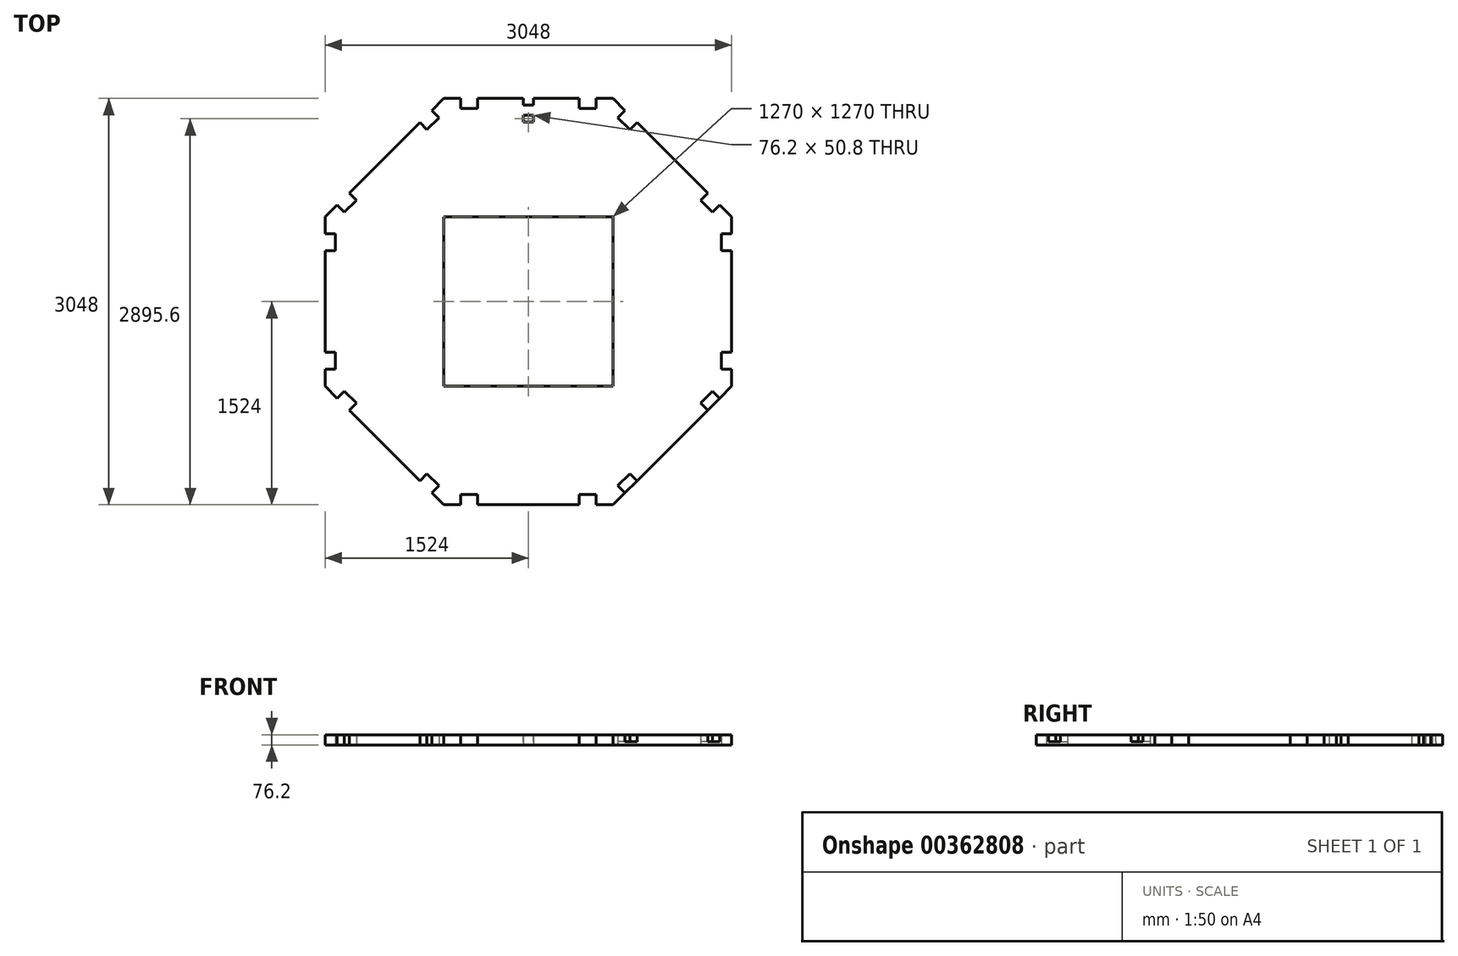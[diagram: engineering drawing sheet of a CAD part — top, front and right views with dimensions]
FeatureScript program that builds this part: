
annotation { "Feature Type Name" : "Feature", "Feature Type Description" : "" }
export const myFeature = defineFeature(function(context is Context, id is Id, definition is map)
    precondition{}
    {
        {
            var Q0;
            Q0=qCreatedBy(makeId("Top.planeOp"),FACE);
            var sketch = newSketch(context, id + "F0", { "sketchPlane" : qUnion([Q0])});
            skLineSegment(sketch, "E0.bottom", {"start": v(-635, 635) * mm, "end": v(635, 635) * mm});
            skLineSegment(sketch, "E0.top", {"start": v(-635, -635) * mm, "end": v(635, -635) * mm});
            skLineSegment(sketch, "E0.left", {"start": v(-1524, 635) * mm, "end": v(-1524, 508) * mm});
            skLineSegment(sketch, "E0.right", {"start": v(1524, 635) * mm, "end": v(1524, 508) * mm});
            skPoint(sketch, "E0.middle", {"position": v(0, 0) * mm});
            skLineSegment(sketch, "E1.bottom", {"start": v(-635, 1524) * mm, "end": v(-508, 1524) * mm});
            skLineSegment(sketch, "E1.top", {"start": v(-635, -1524) * mm, "end": v(-508, -1524) * mm});
            skLineSegment(sketch, "E1.left", {"start": v(-635, 635) * mm, "end": v(-635, -635) * mm});
            skLineSegment(sketch, "E1.right", {"start": v(635, 635) * mm, "end": v(635, -635) * mm});
            skLineSegment(sketch, "E2", {"start": v(-635, 1524) * mm, "end": v(-724.8, 1434.2) * mm});
            skLineSegment(sketch, "E3", {"start": v(-1524, -635) * mm, "end": v(-1434.2, -724.8) * mm});
            skLineSegment(sketch, "E4", {"start": v(635, -1524) * mm, "end": v(1524, -635) * mm});
            skLineSegment(sketch, "E5", {"start": v(1524, 635) * mm, "end": v(1434.2, 724.8) * mm});
            skLineSegment(sketch, "E6", {"start": v(-508, 1524) * mm, "end": v(-508, 1447.8) * mm});
            skLineSegment(sketch, "E7", {"start": v(-508, 1447.8) * mm, "end": v(-381, 1447.8) * mm});
            skLineSegment(sketch, "E8", {"start": v(-381, 1447.8) * mm, "end": v(-381, 1524) * mm});
            skLineSegment(sketch, "E9", {"start": v(635, 1524) * mm, "end": v(508, 1524) * mm});
            skLineSegment(sketch, "E10", {"start": v(508, 1524) * mm, "end": v(508, 1447.8) * mm});
            skLineSegment(sketch, "E11", {"start": v(508, 1447.8) * mm, "end": v(381, 1447.8) * mm});
            skLineSegment(sketch, "E12", {"start": v(381, 1447.8) * mm, "end": v(381, 1524) * mm});
            skLineSegment(sketch, "E13", {"start": v(-38.1, 1524) * mm, "end": v(-38.1, 1473.2) * mm});
            skLineSegment(sketch, "E14", {"start": v(38.1, 1524) * mm, "end": v(38.1, 1473.2) * mm});
            skLineSegment(sketch, "E15", {"start": v(38.1, 1473.2) * mm, "end": v(-38.1, 1473.2) * mm});
            skLineSegment(sketch, "E16", {"start": v(-38.1, 1473.2) * mm, "end": v(-38.1, 1397) * mm});
            skLineSegment(sketch, "E17", {"start": v(38.1, 1473.2) * mm, "end": v(38.1, 1397) * mm});
            skLineSegment(sketch, "E18", {"start": v(38.1, 1397) * mm, "end": v(-38.1, 1397) * mm});
            skLineSegment(sketch, "E19", {"start": v(-38.1, 1397) * mm, "end": v(-38.1, 1346.2) * mm});
            skLineSegment(sketch, "E20", {"start": v(38.1, 1397) * mm, "end": v(38.1, 1346.2) * mm});
            skLineSegment(sketch, "E21", {"start": v(38.1, 1346.2) * mm, "end": v(-38.1, 1346.2) * mm});
            skLineSegment(sketch, "E22", {"start": v(-38.1, 1397) * mm, "end": v(38.1, 1397) * mm});
            skLineSegment(sketch, "E23.trimOffspring", {"start": v(-381, 1524) * mm, "end": v(-38.1, 1524) * mm});
            skLineSegment(sketch, "E24.trimOffspring", {"start": v(508, 1524) * mm, "end": v(635, 1524) * mm});
            skLineSegment(sketch, "E25.trimOffspring", {"start": v(38.1, 1524) * mm, "end": v(381, 1524) * mm});
            skPoint(sketch, "E26.orphan", {"position": v(0, 1524) * mm});
            skLineSegment(sketch, "E27", {"start": v(-1524, 635) * mm, "end": v(-1434.2, 724.8) * mm});
            skLineSegment(sketch, "E28", {"start": v(-1434.2, 724.8) * mm, "end": v(-1380.32, 670.92) * mm});
            skLineSegment(sketch, "E29", {"start": v(-1380.32, 670.92) * mm, "end": v(-1290.51, 760.72) * mm});
            skLineSegment(sketch, "E30", {"start": v(-1290.51, 760.72) * mm, "end": v(-1344.4, 814.6) * mm});
            skLineSegment(sketch, "E31.trimOffspring", {"start": v(-1434.2, 724.8) * mm, "end": v(-1524, 635) * mm});
            skLineSegment(sketch, "E32", {"start": v(-724.8, 1434.2) * mm, "end": v(-670.92, 1380.32) * mm});
            skLineSegment(sketch, "E33", {"start": v(-670.92, 1380.32) * mm, "end": v(-760.72, 1290.51) * mm});
            skLineSegment(sketch, "E34", {"start": v(-760.72, 1290.51) * mm, "end": v(-814.6, 1344.4) * mm});
            skLineSegment(sketch, "E35.trimOffspring", {"start": v(-814.6, 1344.4) * mm, "end": v(-1344.4, 814.6) * mm});
            skLineSegment(sketch, "E36", {"start": v(635, 1524) * mm, "end": v(724.8, 1434.2) * mm});
            skLineSegment(sketch, "E37", {"start": v(724.8, 1434.2) * mm, "end": v(670.92, 1380.32) * mm});
            skLineSegment(sketch, "E38", {"start": v(670.92, 1380.32) * mm, "end": v(760.72, 1290.51) * mm});
            skLineSegment(sketch, "E39", {"start": v(760.72, 1290.51) * mm, "end": v(814.6, 1344.4) * mm});
            skLineSegment(sketch, "E40.trimOffspring", {"start": v(724.8, 1434.2) * mm, "end": v(635, 1524) * mm});
            skLineSegment(sketch, "E41", {"start": v(1434.2, 724.8) * mm, "end": v(1380.32, 670.92) * mm});
            skLineSegment(sketch, "E42", {"start": v(1380.32, 670.92) * mm, "end": v(1290.51, 760.72) * mm});
            skLineSegment(sketch, "E43", {"start": v(1290.51, 760.72) * mm, "end": v(1344.4, 814.6) * mm});
            skLineSegment(sketch, "E44.trimOffspring", {"start": v(1344.4, 814.6) * mm, "end": v(814.6, 1344.4) * mm});
            skLineSegment(sketch, "E45", {"start": v(-38.1, 1473.2) * mm, "end": v(38.1, 1473.2) * mm});
            skLineSegment(sketch, "E46", {"start": v(-1524, 508) * mm, "end": v(-1447.8, 508) * mm});
            skLineSegment(sketch, "E47", {"start": v(-1447.8, 508) * mm, "end": v(-1447.8, 381) * mm});
            skLineSegment(sketch, "E48", {"start": v(-1447.8, 381) * mm, "end": v(-1524, 381) * mm});
            skLineSegment(sketch, "E49.trimOffspring", {"start": v(-1524, 381) * mm, "end": v(-1524, -381) * mm});
            skLineSegment(sketch, "E50", {"start": v(-1524, -635) * mm, "end": v(-1524, -508) * mm});
            skLineSegment(sketch, "E51", {"start": v(-1524, -508) * mm, "end": v(-1447.8, -508) * mm});
            skLineSegment(sketch, "E52", {"start": v(-1447.8, -508) * mm, "end": v(-1447.8, -381) * mm});
            skLineSegment(sketch, "E53", {"start": v(-1447.8, -381) * mm, "end": v(-1524, -381) * mm});
            skLineSegment(sketch, "E54.trimOffspring", {"start": v(-1524, -508) * mm, "end": v(-1524, -635) * mm});
            skLineSegment(sketch, "E55", {"start": v(0, 1524) * mm, "end": v(0, 1397) * mm});
            skLineSegment(sketch, "E56.MirrorCS", {"start": v(1524, 508) * mm, "end": v(1447.8, 508) * mm});
            skLineSegment(sketch, "E57.MirrorCS", {"start": v(1434.2, 724.8) * mm, "end": v(1524, 635) * mm});
            skLineSegment(sketch, "E58.MirrorCS", {"start": v(1524, -508) * mm, "end": v(1524, -635) * mm});
            skLineSegment(sketch, "E59.MirrorCS", {"start": v(1524, -635) * mm, "end": v(1524, -508) * mm});
            skLineSegment(sketch, "E60.MirrorCS", {"start": v(1524, -508) * mm, "end": v(1447.8, -508) * mm});
            skLineSegment(sketch, "E61.MirrorCS", {"start": v(1447.8, 508) * mm, "end": v(1447.8, 381) * mm});
            skLineSegment(sketch, "E62.MirrorCS", {"start": v(1447.8, 381) * mm, "end": v(1524, 381) * mm});
            skLineSegment(sketch, "E63.MirrorCS", {"start": v(1447.8, -381) * mm, "end": v(1524, -381) * mm});
            skLineSegment(sketch, "E64.MirrorCS", {"start": v(1447.8, -508) * mm, "end": v(1447.8, -381) * mm});
            skLineSegment(sketch, "E65.MirrorCS", {"start": v(381, 1524) * mm, "end": v(38.1, 1524) * mm});
            skLineSegment(sketch, "E66.MirrorCS", {"start": v(1524, -635) * mm, "end": v(635, -1524) * mm});
            skLineSegment(sketch, "E67.MirrorCS", {"start": v(814.6, 1344.4) * mm, "end": v(1344.4, 814.6) * mm});
            skLineSegment(sketch, "E68.MirrorCS", {"start": v(1524, 381) * mm, "end": v(1524, -381) * mm});
            skLineSegment(sketch, "E69", {"start": v(-1434.2, -724.8) * mm, "end": v(-1524, -635) * mm});
            skLineSegment(sketch, "E70", {"start": v(-1434.2, -724.8) * mm, "end": v(-1380.32, -670.92) * mm});
            skLineSegment(sketch, "E71", {"start": v(-1380.32, -670.92) * mm, "end": v(-1290.51, -760.72) * mm});
            skLineSegment(sketch, "E72", {"start": v(-1290.51, -760.72) * mm, "end": v(-1344.4, -814.6) * mm});
            skLineSegment(sketch, "E73.trimOffspring", {"start": v(-1344.4, -814.6) * mm, "end": v(-814.6, -1344.4) * mm});
            skLineSegment(sketch, "E74", {"start": v(-635, -1524) * mm, "end": v(-724.8, -1434.2) * mm});
            skLineSegment(sketch, "E75", {"start": v(-724.8, -1434.2) * mm, "end": v(-670.92, -1380.32) * mm});
            skLineSegment(sketch, "E76", {"start": v(-670.92, -1380.32) * mm, "end": v(-760.72, -1290.51) * mm});
            skLineSegment(sketch, "E77", {"start": v(-760.72, -1290.51) * mm, "end": v(-814.6, -1344.4) * mm});
            skLineSegment(sketch, "E78.trimOffspring", {"start": v(-724.8, -1434.2) * mm, "end": v(-635, -1524) * mm});
            skLineSegment(sketch, "E79.MirrorCS", {"start": v(635, -1524) * mm, "end": v(724.8, -1434.2) * mm});
            skLineSegment(sketch, "E80.MirrorCS", {"start": v(724.8, -1434.2) * mm, "end": v(635, -1524) * mm});
            skLineSegment(sketch, "E81.MirrorCS", {"start": v(1434.2, -724.8) * mm, "end": v(1524, -635) * mm});
            skLineSegment(sketch, "E82.MirrorCS", {"start": v(1434.2, -724.8) * mm, "end": v(1380.32, -670.92) * mm});
            skLineSegment(sketch, "E83.MirrorCS", {"start": v(1290.51, -760.72) * mm, "end": v(1344.4, -814.6) * mm});
            skLineSegment(sketch, "E84.MirrorCS", {"start": v(1380.32, -670.92) * mm, "end": v(1290.51, -760.72) * mm});
            skLineSegment(sketch, "E85.MirrorCS", {"start": v(1524, -635) * mm, "end": v(1434.2, -724.8) * mm});
            skLineSegment(sketch, "E86.MirrorCS", {"start": v(1344.4, -814.6) * mm, "end": v(814.6, -1344.4) * mm});
            skLineSegment(sketch, "E87", {"start": v(814.6, -1344.4) * mm, "end": v(724.8, -1434.2) * mm});
            skLineSegment(sketch, "E88", {"start": v(-508, -1524) * mm, "end": v(-508, -1447.8) * mm});
            skLineSegment(sketch, "E89", {"start": v(-508, -1447.8) * mm, "end": v(-381, -1447.8) * mm});
            skLineSegment(sketch, "E90", {"start": v(-381, -1447.8) * mm, "end": v(-381, -1524) * mm});
            skLineSegment(sketch, "E91.MirrorCS", {"start": v(508, -1524) * mm, "end": v(508, -1447.8) * mm});
            skLineSegment(sketch, "E92.MirrorCS", {"start": v(381, -1447.8) * mm, "end": v(381, -1524) * mm});
            skLineSegment(sketch, "E93.MirrorCS", {"start": v(635, -1524) * mm, "end": v(508, -1524) * mm});
            skLineSegment(sketch, "E94.MirrorCS", {"start": v(508, -1447.8) * mm, "end": v(381, -1447.8) * mm});
            skLineSegment(sketch, "E95.trimOffspring", {"start": v(508, -1524) * mm, "end": v(635, -1524) * mm});
            skLineSegment(sketch, "E96.trimOffspring", {"start": v(-381, -1524) * mm, "end": v(381, -1524) * mm});
            skLineSegment(sketch, "E97.trimOffspring", {"start": v(-381, -1524) * mm, "end": v(0, -1524) * mm});
            skLineSegment(sketch, "E98.trimOffspring", {"start": v(381, -1524) * mm, "end": v(0, -1524) * mm});
            skPoint(sketch, "E99.MirrorCS.end.orphan", {"position": v(760.72, -1290.51) * mm});
            skPoint(sketch, "E100.MirrorCS.end.orphan", {"position": v(670.92, -1380.32) * mm});
            skLineSegment(sketch, "E101", {"start": v(670.92, -1380.32) * mm, "end": v(724.8, -1434.2) * mm});
            skLineSegment(sketch, "E102", {"start": v(760.72, -1290.51) * mm, "end": v(814.6, -1344.4) * mm});
            skLineSegment(sketch, "E103", {"start": v(760.72, -1290.51) * mm, "end": v(670.92, -1380.32) * mm});
            skSolve(sketch);
        }
        {
            var Q0;
            Q0 = qSketchRegion(id + "F0", true);
            extrude(context, id + "F1", {"entities" : qUnion([Q0]), "depth" : 25.4 * mm});
        }
        {
            var Q0;
            Q0=makeQuery(id+"F0.imprint","IMPRINT",FACE,{"disambiguationData":[TD([[makeQuery(id+"F0.imprint","IMPRINT",EDGE,{"derivedFrom":sQuery(id+"F0.wireOp",EDGE,"E66.MirrorCS")}),-1.0]])]});
            var Q1;
            Q1=makeQuery(id+"F0.imprint","IMPRINT",FACE,{"disambiguationData":[TD([[makeQuery(id+"F0.imprint","IMPRINT",EDGE,{"derivedFrom":sQuery(id+"F0.wireOp",EDGE,"E87")}),-1.0]])]});
            var Q2;
            {var subQ0=sQuery(id+"F0.wireOp",EDGE,"E16");Q2=makeQuery(id+"F0.imprint","IMPRINT",FACE,{"disambiguationData":[TD([[makeQuery(id+"F0.imprint","IMPRINT",EDGE,{"derivedFrom":subQ0}),1.0]])]});}
            var Q3;
            {var subQ0=sQuery(id+"F0.wireOp",EDGE,"E17");Q3=makeQuery(id+"F0.imprint","IMPRINT",FACE,{"disambiguationData":[TD([[makeQuery(id+"F0.imprint","IMPRINT",EDGE,{"derivedFrom":subQ0}),-1.0]])]});}
            var Q4;
            Q4=makeQuery(id+"F0.imprint","IMPRINT",FACE,{"disambiguationData":[TD([[makeQuery(id+"F0.imprint","IMPRINT",EDGE,{"derivedFrom":sQuery(id+"F0.wireOp",EDGE,"E17")}),1.0]])]});
            extrude(context, id + "F2", {"entities" : qUnion([Q0, Q1, Q2, Q3, Q4]), "operationType" : NewBodyOperationType.ADD, "depth" : 76.2 * mm});
        }
    });
